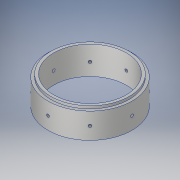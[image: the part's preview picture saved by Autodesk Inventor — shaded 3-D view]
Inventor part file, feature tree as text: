
AUTODESK INVENTOR PART (.ipt)
format: ipt  version: 2017 SP1 (Build 210196100, 196)  size: 190,976 bytes
history: native  units: in
note: dims shown in document units (in); Inventor stores cm internally (conversion verified against a paired STEP export)
features: sketch x2, revolve x1, plane x1, hole x1, pattern_circular x1
ambient origin geometry x8: Origin, YZ Plane, XZ Plane, XY Plane, X Axis, Y Axis, Z Axis, Center Point
bodies: Solid1 (feature_tree)
feature tree (6):
  revolve  "Revolution1"  [1 undecoded]
  plane  "Work Plane1"
  hole  "Hole1"  [1 undecoded]
  pattern_circular  "Circular Pattern1"  [2 undecoded]
  sketch  "Sketch1"  dims[d0=1.13in d1=3.75in]
  sketch  "Sketch2"  dims[d2=0.125in d3=0.1718in d5=1.0in d6=1.0in d7=90.0deg d8=0.5in d9=15.0deg d12=1.25in d13=0.25in d16=0.5in d17=0.5in d18=0.5in d19=2.5in d20=0.5in d22=0.375in d23=0.25in d25=0.234in d27=0.125in d28=0.25in d29=1.0in d30=4.25in d31=0.25in d33=0.8014in d34=15.0deg d35=0.125in d36=1.0in d37=90.0deg d38=0.25in d39=0.75in d40=0.375in d41=0.25in d42=0.5635in d43=1.0in d44=0.8108in d45=3.1496in d46=360.0deg]
note: 4 required parameter values undecoded (feature->parameter linkage not recoverable at this tier; creation-order binding heuristic only, values carry confidence <= 0.55)